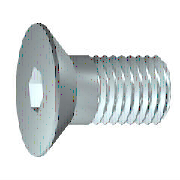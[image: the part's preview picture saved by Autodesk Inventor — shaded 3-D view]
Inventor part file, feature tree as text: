
AUTODESK INVENTOR PART (.ipt)
format: ipt  version: 2015 (Build 190159000, 159)  size: 180,224 bytes
history: native  units: mm (DEFAULTED — no unit token found)
features: sketch x2, extrude x1, plane x1
ambient origin geometry x7: Origin, YZ Plane, XY Plane, X Axis, Y Axis, Z Axis, Center Point
bodies: Solid1 (feature_tree), Body (feature_tree)
feature tree (4):
  sketch  "Sketch2"  dims[d2=2.67mm d3=6.0mm d6=3.72mm d7=45.0deg d8=4.618802mm d9=60.0deg d10=11.34mm d11=6.0mm d12=0.61345mm d13=90.0deg d30=10.0mm d14=0.0mm d15=18.0mm d16=0.0mm d17=0.61345mm d18=0.61345mm d20=0.0mm d39=45.0deg d43=0.0mm d44=0.0mm]
  extrude  "Slot"  Depth=18.0mm
  plane  "Work Plane1"
  sketch  "Sketch1"  dims[d0=25.0mm d1=18.0mm]
